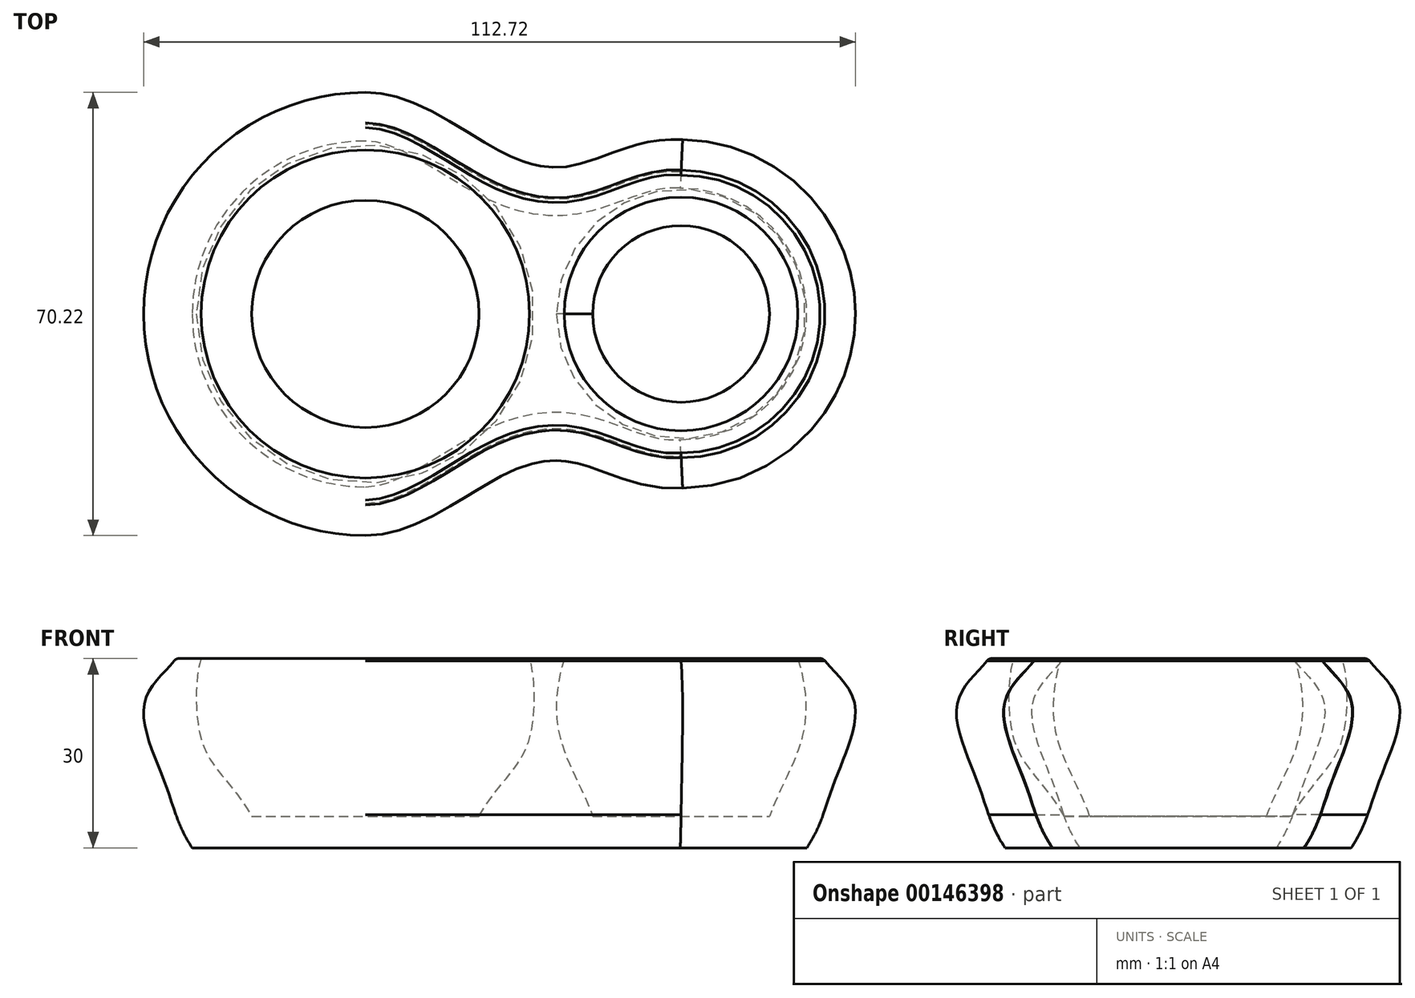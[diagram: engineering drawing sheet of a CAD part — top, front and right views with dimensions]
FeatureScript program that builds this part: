
annotation { "Feature Type Name" : "Feature", "Feature Type Description" : "" }
export const myFeature = defineFeature(function(context is Context, id is Id, definition is map)
    precondition{}
    {
        {
            var Q0;
            Q0=qCreatedBy(makeId("Top.planeOp"),FACE);
            var sketch = newSketch(context, id + "F0", { "sketchPlane" : qUnion([Q0])});
            skArc(sketch, "E0", {"start": v(0, 30) * mm, "mid": v(-21.21, 21.21) * mm, "end": v(-30, 0) * mm});
            skArc(sketch, "E1", {"start": v(50, -22.5) * mm, "mid": v(72.5, 0) * mm, "end": v(50, 22.5) * mm});
            skLineSegment(sketch, "E2", {"start": v(0, 0) * mm, "end": v(50, 0) * mm, "construction": true});
            skFitSpline(sketch, "E3", {"points": [v(0, 30) * mm, v(19.6, 20.93) * mm, v(34.6, 18.66) * mm, v(50, 22.5) * mm], "startDerivative": vector(51.3, 0.17) * mm, "endDerivative": vector(50, -5) * mm});
            skFitSpline(sketch, "E4.MirrorCS", {"points": [v(0, -30) * mm, v(19.6, -20.93) * mm, v(34.6, -18.66) * mm, v(50, -22.5) * mm], "startDerivative": vector(51.3, -0.17) * mm, "endDerivative": vector(50, 5) * mm});
            skLineSegment(sketch, "E5", {"start": v(0, 0) * mm, "end": v(-30, 0) * mm, "construction": true});
            skArc(sketch, "E6", {"start": v(-30, 0) * mm, "mid": v(-21.21, -21.21) * mm, "end": v(0, -30) * mm});
            skSolve(sketch);
        }
        {
            var Q0;
            Q0 = qSketchRegion(id + "F0", true);
            extrude(context, id + "F1", {"entities" : qUnion([Q0]), "oppositeDirection" : true, "depth" : 30 * mm});
        }
        {
            var Q0;
            Q0=qCreatedBy(makeId("Front.planeOp"),FACE);
            var sketch = newSketch(context, id + "F2", { "sketchPlane" : qUnion([Q0])});
            skPoint(sketch, "E7.0", {"position": v(0, 0) * mm});
            skPoint(sketch, "E7.1", {"position": v(50, 0) * mm});
            skPoint(sketch, "E8.0", {"position": v(-30, 0) * mm});
            skPoint(sketch, "E9.0.end.orphan", {"position": v(72.5, 0) * mm});
            skLineSegment(sketch, "E10", {"start": v(0, 0) * mm, "end": v(0, -25) * mm});
            skLineSegment(sketch, "E11", {"start": v(-30, 0) * mm, "end": v(-26, 0) * mm, "construction": true});
            skLineSegment(sketch, "E12", {"start": v(-26, 0) * mm, "end": v(0, 0) * mm});
            skLineSegment(sketch, "E13", {"start": v(0, -25) * mm, "end": v(-18, -25) * mm});
            skFitSpline(sketch, "E14", {"points": [v(-26, 0) * mm, v(-25.85, -13.23) * mm, v(-18, -25) * mm], "startDerivative": vector(-5.42, -15.01) * mm, "endDerivative": vector(18.97, -33.16) * mm});
            skLineSegment(sketch, "E15", {"start": v(72.5, 0) * mm, "end": v(68.5, 0) * mm, "construction": true});
            skLineSegment(sketch, "E16", {"start": v(50, 0) * mm, "end": v(68.5, 0) * mm});
            skLineSegment(sketch, "E17", {"start": v(50, 0) * mm, "end": v(50, -25) * mm});
            skLineSegment(sketch, "E18", {"start": v(50, -25) * mm, "end": v(64, -25) * mm});
            skFitSpline(sketch, "E19", {"points": [v(68.5, 0) * mm, v(68.95, -13.3) * mm, v(64, -25) * mm], "startDerivative": vector(9.26, -30.36) * mm, "endDerivative": vector(-9.1, -25.75) * mm});
            skSolve(sketch);
        }
        {
            var Q0;
            Q0=makeQuery(id+"F2.imprint","IMPRINT",FACE,{"disambiguationData":[TD([[makeQuery(id+"F2.imprint","IMPRINT",EDGE,{"derivedFrom":sQuery(id+"F2.wireOp",EDGE,"E10")}),-1.0]])]});
            var Q1;
            Q1=sQuery(id+"F2.wireOp",EDGE,"E10");
            revolve(context, id + "F3", {"operationType" : NewBodyOperationType.REMOVE, "entities" : qUnion([Q0]), "axis" : qUnion([Q1]), "revolveType" : RevolveType.FULL, "oppositeDirection" : true});
        }
        {
            var Q0;
            Q0=makeQuery(id+"F2.imprint","IMPRINT",FACE,{"disambiguationData":[TD([[makeQuery(id+"F2.imprint","IMPRINT",EDGE,{"derivedFrom":sQuery(id+"F2.wireOp",EDGE,"E16")}),-1.0]])]});
            var Q1;
            Q1=sQuery(id+"F2.wireOp",EDGE,"E17");
            revolve(context, id + "F4", {"operationType" : NewBodyOperationType.REMOVE, "entities" : qUnion([Q0]), "axis" : qUnion([Q1]), "revolveType" : RevolveType.FULL, "oppositeDirection" : true});
        }
        {
            var Q0;
            Q0=qCreatedBy(makeId("Front.planeOp"),FACE);
            var sketch = newSketch(context, id + "F5", { "sketchPlane" : qUnion([Q0])});
            skLineSegment(sketch, "E20.1", {"start": v(-27.41, -30) * mm, "end": v(-30, -30) * mm});
            skFitSpline(sketch, "E21", {"points": [v(-30, 0) * mm, v(-34.98, -7.11) * mm, v(-31.66, -19.87) * mm, v(-27.41, -30) * mm], "startDerivative": vector(-15.88, -21.18) * mm, "endDerivative": vector(21.77, -32.87) * mm});
            skLineSegment(sketch, "E22", {"start": v(-30, 0) * mm, "end": v(-30, -24.76) * mm});
            skLineSegment(sketch, "E23", {"start": v(-30, -24.76) * mm, "end": v(-30, -30) * mm});
            skPoint(sketch, "E20.0.start.orphan", {"position": v(0, 0) * mm});
            skPoint(sketch, "E24.orphan", {"position": v(0, -30) * mm});
            skSolve(sketch);
        }
        {
            var Q0;
            {var subQ0=sQuery(id+"F5.wireOp",EDGE,"E22");Q0=makeQuery(id+"F5.imprint","IMPRINT",FACE,{"disambiguationData":[TD([[makeQuery(id+"F5.imprint","IMPRINT",EDGE,{"derivedFrom":subQ0}),-1.0]])]});}
            var Q1;
            Q1 = qConstructionFilter(qBodyType(qCreatedBy(id + "F0" ,EDGE), BodyType.WIRE), ConstructionObject.NO);
            sweep(context, id + "F6", {"operationType" : NewBodyOperationType.ADD, "profiles" : qUnion([Q0]), "path" : qUnion([Q1])});
        }
        {
            var Q0;
            {var subQ0=sQuery(id+"F5.wireOp",EDGE,"E20.1");Q0=makeQuery(id+"F5.imprint","IMPRINT",FACE,{"disambiguationData":[TD([[makeQuery(id+"F5.imprint","IMPRINT",EDGE,{"derivedFrom":subQ0}),-1.0]])]});}
            var Q1;
            Q1 = qConstructionFilter(qBodyType(qCreatedBy(id + "F0" ,EDGE), BodyType.WIRE), ConstructionObject.NO);
            sweep(context, id + "F7", {"operationType" : NewBodyOperationType.REMOVE, "profiles" : qUnion([Q0]), "path" : qUnion([Q1])});
        }
        {
            var Q0;
            Q0=makeQuery(id+"F3.boolean.opBoolean","COPY",EDGE,{"derivedFrom":makeQuery(id+"F3.opRevolve","SWEPT_EDGE",EDGE,{"disambiguationData":[OSD([sQuery(id+"F2.wireOp",EDGE,"E12"),sQuery(id+"F2.wireOp",EDGE,"E14")])]})});
            var Q1;
            {var subQ0=sQuery(id+"F0.wireOp",EDGE,"E0");Q1=makeQuery(id+"F6.boolean.opBoolean","MERGE",EDGE,{"derivedFrom":[makeQuery(id+"F1.opExtrude","CAP_EDGE",EDGE,{"disambiguationData":[OSD([subQ0,sQuery(id+"F0.wireOp",EDGE,"E6")])],"isStart":true}),makeQuery(id+"F6.opSweep","SWEPT_EDGE",EDGE,{"disambiguationData":[OSD([subQ0,sQuery(id+"F5.wireOp",EDGE,"E21"),sQuery(id+"F5.wireOp",EDGE,"E22")])]})]});}
            var Q2;
            {var subQ0=sQuery(id+"F0.wireOp",EDGE,"E3");Q2=makeQuery(id+"F6.boolean.opBoolean","MERGE",EDGE,{"derivedFrom":[makeQuery(id+"F1.opExtrude","CAP_EDGE",EDGE,{"disambiguationData":[OSD([subQ0])],"isStart":true}),makeQuery(id+"F6.opSweep","SWEPT_EDGE",EDGE,{"disambiguationData":[OSD([subQ0,sQuery(id+"F5.wireOp",EDGE,"E21"),sQuery(id+"F5.wireOp",EDGE,"E22")])]})]});}
            var Q3;
            Q3=makeQuery(id+"F4.boolean.opBoolean","COPY",EDGE,{"derivedFrom":makeQuery(id+"F4.opRevolve","SWEPT_EDGE",EDGE,{"disambiguationData":[OSD([sQuery(id+"F2.wireOp",EDGE,"E16"),sQuery(id+"F2.wireOp",EDGE,"E19")])]})});
            var Q4;
            {var subQ0=sQuery(id+"F0.wireOp",EDGE,"E1");Q4=makeQuery(id+"F6.boolean.opBoolean","MERGE",EDGE,{"derivedFrom":[makeQuery(id+"F1.opExtrude","CAP_EDGE",EDGE,{"disambiguationData":[OSD([subQ0])],"isStart":true}),makeQuery(id+"F6.opSweep","SWEPT_EDGE",EDGE,{"disambiguationData":[OSD([subQ0,sQuery(id+"F5.wireOp",EDGE,"E21"),sQuery(id+"F5.wireOp",EDGE,"E22")])]})]});}
            var Q5;
            {var subQ0=sQuery(id+"F0.wireOp",EDGE,"E4.MirrorCS");Q5=makeQuery(id+"F6.boolean.opBoolean","MERGE",EDGE,{"derivedFrom":[makeQuery(id+"F1.opExtrude","CAP_EDGE",EDGE,{"disambiguationData":[OSD([subQ0])],"isStart":true}),makeQuery(id+"F6.opSweep","SWEPT_EDGE",EDGE,{"disambiguationData":[OSD([subQ0,sQuery(id+"F5.wireOp",EDGE,"E21"),sQuery(id+"F5.wireOp",EDGE,"E22")])]})]});}
            var Q6;
            {var subQ0=sQuery(id+"F0.wireOp",EDGE,"E6");Q6=makeQuery(id+"F6.boolean.opBoolean","MERGE",EDGE,{"derivedFrom":[makeQuery(id+"F1.opExtrude","CAP_EDGE",EDGE,{"disambiguationData":[OSD([sQuery(id+"F0.wireOp",EDGE,"E0"),subQ0])],"isStart":true}),makeQuery(id+"F6.opSweep","SWEPT_EDGE",EDGE,{"disambiguationData":[OSD([subQ0,sQuery(id+"F5.wireOp",EDGE,"E21"),sQuery(id+"F5.wireOp",EDGE,"E22")])]})]});}
            fillet(context, id + "F8", {"entities" : qUnion([Q0, Q1, Q2, Q3, Q4, Q5, Q6]), "radius" : 1 * mm, "tangentPropagation" : true, "allowEdgeOverflow" : false});
        }
    });
